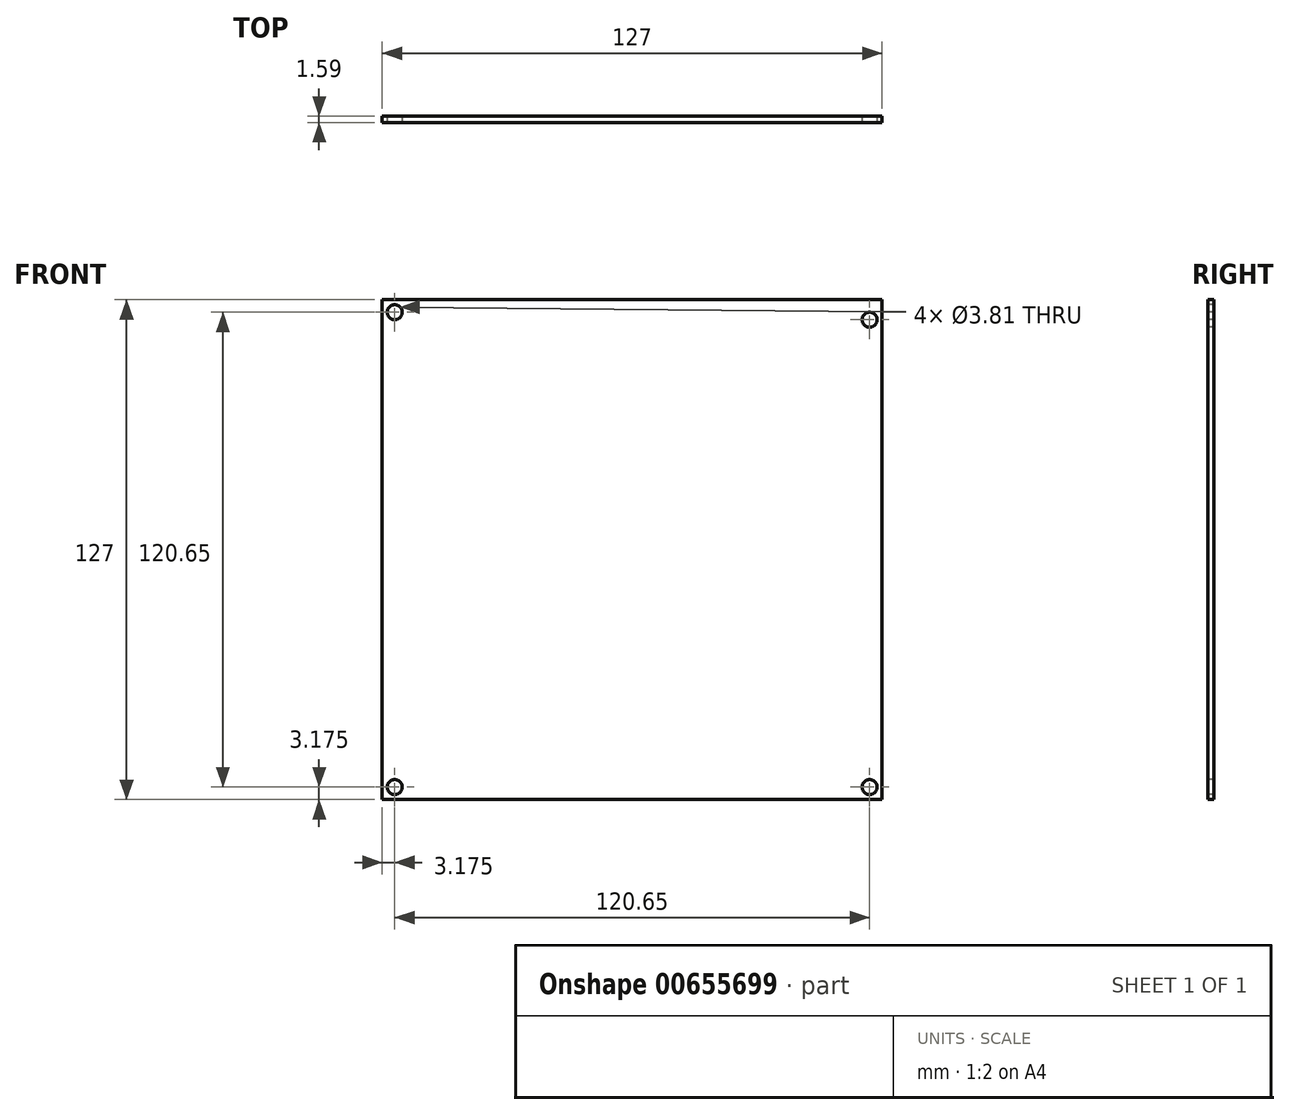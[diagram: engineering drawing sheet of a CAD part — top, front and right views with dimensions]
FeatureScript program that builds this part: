
annotation { "Feature Type Name" : "Feature", "Feature Type Description" : "" }
export const myFeature = defineFeature(function(context is Context, id is Id, definition is map)
    precondition{}
    {
        {
            var Q0;
            Q0=qCreatedBy(makeId("Front.planeOp"),FACE);
            var sketch = newSketch(context, id + "F0", { "sketchPlane" : qUnion([Q0])});
            skLineSegment(sketch, "E0.bottom", {"start": v(63.5, -63.5) * mm, "end": v(-63.5, -63.5) * mm});
            skLineSegment(sketch, "E0.top", {"start": v(63.5, 63.5) * mm, "end": v(-63.5, 63.5) * mm});
            skLineSegment(sketch, "E0.left", {"start": v(63.5, -63.5) * mm, "end": v(63.5, 63.5) * mm});
            skLineSegment(sketch, "E0.right", {"start": v(-63.5, -63.5) * mm, "end": v(-63.5, 63.5) * mm});
            skPoint(sketch, "E0.middle", {"position": v(0, 0) * mm});
            skSolve(sketch);
        }
        {
            var Q0;
            Q0 = qSketchRegion(id + "F0", true);
            extrude(context, id + "F1", {"entities" : qUnion([Q0]), "oppositeDirection" : true, "depth" : 1.59 * mm, "offsetDistance" : 25.4 * mm});
        }
        {
            var Q0;
            Q0=makeQuery(id+"F1.opExtrude","CAP_FACE",FACE,{"disambiguationData":[OSD([sQuery(id+"F0.wireOp",EDGE,"E0.bottom"),sQuery(id+"F0.wireOp",EDGE,"E0.top"),sQuery(id+"F0.wireOp",EDGE,"E0.left"),sQuery(id+"F0.wireOp",EDGE,"E0.right")])],"isStart":true});
            var sketch = newSketch(context, id + "F2", { "sketchPlane" : qUnion([Q0])});
            skCircle(sketch, "E1", {"center": v(-60.33, 60.32) * mm, "radius": 1.9 * mm});
            skCircle(sketch, "E2", {"center": v(60.33, 58.42) * mm, "radius": 1.9 * mm});
            skCircle(sketch, "E3", {"center": v(-60.33, -60.33) * mm, "radius": 1.9 * mm});
            skCircle(sketch, "E4", {"center": v(60.32, -60.33) * mm, "radius": 1.9 * mm});
            skSolve(sketch);
        }
        {
            var Q0;
            Q0 = qSketchRegion(id + "F2", true);
            extrude(context, id + "F3", {"entities" : qUnion([Q0]), "operationType" : NewBodyOperationType.REMOVE, "oppositeDirection" : true, "depth" : 25.4 * mm, "offsetDistance" : 25.4 * mm});
        }
    });
